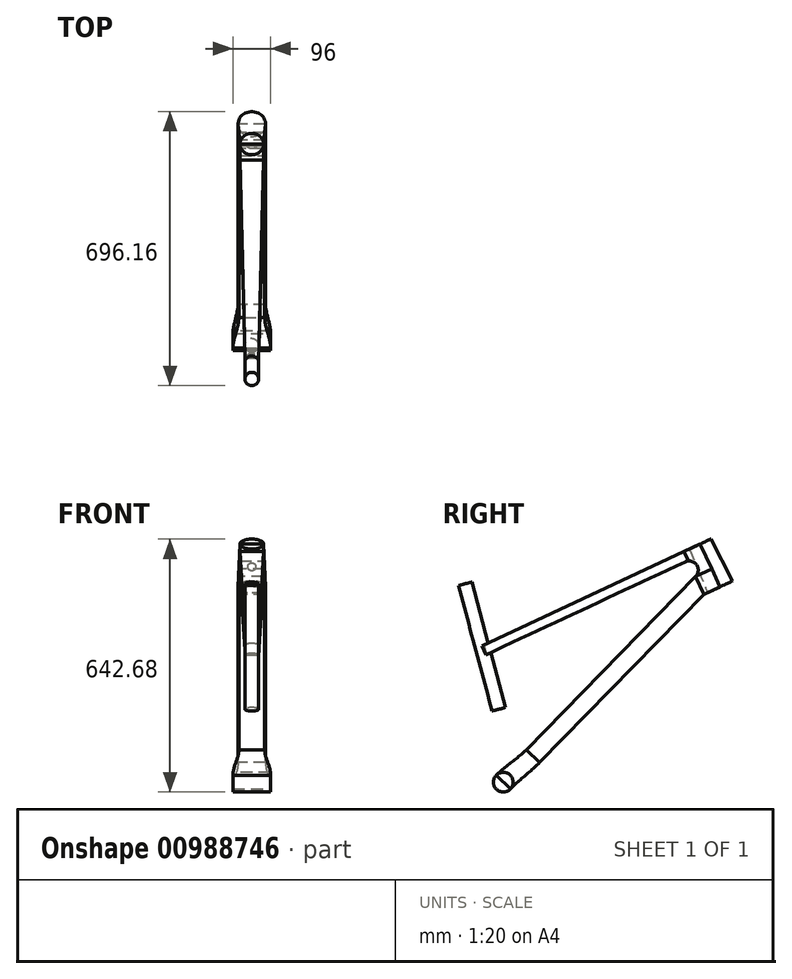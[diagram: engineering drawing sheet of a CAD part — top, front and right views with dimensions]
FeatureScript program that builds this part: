
annotation { "Feature Type Name" : "Feature", "Feature Type Description" : "" }
export const myFeature = defineFeature(function(context is Context, id is Id, definition is map)
    precondition{}
    {
        {
            var Q0;
            Q0=qCreatedBy(makeId("Right.planeOp"),FACE);
            var sketch = newSketch(context, id + "F0", { "sketchPlane" : qUnion([Q0])});
            skLineSegment(sketch, "E0", {"start": v(30, 30.68) * mm, "end": v(-96.82, 503.98) * mm});
            skCircle(sketch, "E1", {"center": v(0, 0) * mm, "radius": 25 * mm});
            skLineSegment(sketch, "E2", {"start": v(0, 0) * mm, "end": v(0, 605) * mm});
            skLineSegment(sketch, "E3", {"start": v(0, 605) * mm, "end": v(500, 605) * mm});
            skLineSegment(sketch, "E4", {"start": v(500, 605) * mm, "end": v(550.71, 496.24) * mm});
            skLineSegment(sketch, "E5", {"start": v(-123.89, 605) * mm, "end": v(500, 605) * mm});
            skLineSegment(sketch, "E6", {"start": v(0, 0) * mm, "end": v(991.3, 0) * mm});
            skLineSegment(sketch, "E7", {"start": v(-96.82, 503.98) * mm, "end": v(-123.89, 605) * mm});
            skLineSegment(sketch, "E8", {"start": v(550.71, 496.24) * mm, "end": v(590.6, 514.84) * mm});
            skLineSegment(sketch, "E9", {"start": v(590.6, 514.84) * mm, "end": v(825.14, 11.84) * mm});
            skLineSegment(sketch, "E10", {"start": v(0, 11.84) * mm, "end": v(-430, 11.84) * mm});
            skCircle(sketch, "E11", {"center": v(-430, 11.84) * mm, "radius": 300 * mm});
            skCircle(sketch, "E12", {"center": v(825.14, 11.84) * mm, "radius": 342 * mm});
            skLineSegment(sketch, "E13", {"start": v(500, 605) * mm, "end": v(-76.95, 429.84) * mm});
            skLineSegment(sketch, "E14", {"start": v(-537.8, -330.16) * mm, "end": v(1117.44, -330.16) * mm});
            skLineSegment(sketch, "E15", {"start": v(500, 605) * mm, "end": v(-54.6, 346.39) * mm});
            skCircle(sketch, "E16", {"center": v(-430, 11.84) * mm, "radius": 362.5 * mm});
            skLineSegment(sketch, "E17", {"start": v(-96.82, 503.98) * mm, "end": v(0, 11.84) * mm, "construction": true});
            skLineSegment(sketch, "E18", {"start": v(0, 0) * mm, "end": v(529.58, 541.56) * mm});
            skCircle(sketch, "E19", {"center": v(0, 0) * mm, "radius": 70 * mm, "construction": true});
            skSolve(sketch);
        }
        {
            var Q0;
            Q0=qCreatedBy(makeId("Right.planeOp"),FACE);
            var sketch = newSketch(context, id + "F1", { "sketchPlane" : qUnion([Q0])});
            skLineSegment(sketch, "E20", {"start": v(500, 605) * mm, "end": v(527.19, 617.68) * mm});
            skLineSegment(sketch, "E21", {"start": v(550.71, 496.24) * mm, "end": v(582.43, 511.03) * mm});
            skLineSegment(sketch, "E22", {"start": v(500, 605) * mm, "end": v(550.71, 496.24) * mm});
            skLineSegment(sketch, "E23", {"start": v(527.19, 617.68) * mm, "end": v(582.43, 511.03) * mm});
            skSolve(sketch);
        }
        {
            var Q0;
            Q0=sQuery(id+"F0.wireOp",EDGE,"E15");
            var Q1;
            Q1=sQuery(id+"F0.wireOp",VERTEX,"E3.end");
            cPlane(context, id + "F2", {"entities" : qUnion([Q0, Q1]), "cplaneType" : CPlaneType.LINE_POINT, "offset" : 25 * mm, "width" : 150 * mm, "height" : 150 * mm});
        }
        {
            var Q0;
            Q0=sQuery(id+"F0.wireOp",EDGE,"E18");
            var Q1;
            Q1=sQuery(id+"F0.wireOp",VERTEX,"E2.start");
            cPlane(context, id + "F3", {"entities" : qUnion([Q0, Q1]), "cplaneType" : CPlaneType.LINE_POINT, "offset" : 25 * mm, "width" : 150 * mm, "height" : 150 * mm});
        }
        {
            var Q0;
            Q0=qCreatedBy(id+"F3.planeOp",FACE);
            var sketch = newSketch(context, id + "F4", { "sketchPlane" : qUnion([Q0])});
            skLineSegment(sketch, "E24.bottom", {"start": v(-48, 25) * mm, "end": v(48, 25) * mm});
            skLineSegment(sketch, "E24.top", {"start": v(-48, -25) * mm, "end": v(48, -25) * mm});
            skLineSegment(sketch, "E24.left", {"start": v(-48, 25) * mm, "end": v(-48, -25) * mm});
            skLineSegment(sketch, "E24.right", {"start": v(48, 25) * mm, "end": v(48, -25) * mm});
            skPoint(sketch, "E24.middle", {"position": v(0, 0) * mm});
            skSolve(sketch);
        }
        {
            var Q0;
            Q0=sQuery(id+"F0.wireOp",VERTEX,"E0.end");
            var Q1;
            Q1=sQuery(id+"F0.wireOp",EDGE,"E0");
            cPlane(context, id + "F5", {"entities" : qUnion([Q0, Q1]), "cplaneType" : CPlaneType.LINE_POINT, "offset" : 25 * mm, "width" : 150 * mm, "height" : 150 * mm});
        }
        {
            var Q0;
            Q0=qCreatedBy(id+"F5.planeOp",FACE);
            var sketch = newSketch(context, id + "F6", { "sketchPlane" : qUnion([Q0])});
            skCircle(sketch, "E25", {"center": v(0, 36.92) * mm, "radius": 17.5 * mm});
            skSolve(sketch);
        }
        {
            var Q0;
            Q0 = qSketchRegion(id + "F1", true);
            var Q1;
            Q1=sQuery(id+"F1.wireOp",EDGE,"E23");
            var Q2;
            Q2=sQuery(id+"F0.wireOp",EDGE,"E4");
            revolve(context, id + "F7", {"surfaceOperationType" : NewSurfaceOperationType.NEW, "entities" : qUnion([Q0]), "surfaceEntities" : qUnion([Q1]), "axis" : qUnion([Q2]), "revolveType" : RevolveType.FULL});
        }
        {
            var Q0;
            {var subQ0=sQuery(id+"F0.wireOp",EDGE,"E2");var subQ1=sQuery(id+"F0.wireOp",EDGE,"E1");var subQ2=makeQuery(id+"F0.imprint","INTERSECT",VERTEX,{"derivedFrom":[subQ1,subQ0]});Q0=makeQuery(id+"F0.imprint","IMPRINT",FACE,{"disambiguationData":[TD([[makeQuery(id+"F0.imprint","IMPRINT",EDGE,{"disambiguationData":[TD([[subQ2,-1.0]])],"derivedFrom":subQ1}),1.0]])]});}
            var Q1;
            {var subQ0=sQuery(id+"F0.wireOp",EDGE,"E2");var subQ1=sQuery(id+"F0.wireOp",EDGE,"E1");var subQ2=makeQuery(id+"F0.imprint","INTERSECT",VERTEX,{"derivedFrom":[subQ1,subQ0]});Q1=makeQuery(id+"F0.imprint","IMPRINT",FACE,{"disambiguationData":[TD([[makeQuery(id+"F0.imprint","IMPRINT",EDGE,{"disambiguationData":[TD([[subQ2,1.0]])],"derivedFrom":subQ1}),1.0]])]});}
            var Q2;
            {var subQ0=sQuery(id+"F0.wireOp",EDGE,"E18");var subQ1=sQuery(id+"F0.wireOp",EDGE,"E1");var subQ2=makeQuery(id+"F0.imprint","INTERSECT",VERTEX,{"derivedFrom":[subQ1,subQ0]});Q2=makeQuery(id+"F0.imprint","IMPRINT",FACE,{"disambiguationData":[TD([[makeQuery(id+"F0.imprint","IMPRINT",EDGE,{"disambiguationData":[TD([[subQ2,1.0]])],"derivedFrom":subQ1}),1.0]])]});}
            var Q3;
            {var subQ0=sQuery(id+"F0.wireOp",EDGE,"E10");var subQ1=sQuery(id+"F0.wireOp",EDGE,"E1");var subQ2=makeQuery(id+"F0.imprint","INTERSECT",VERTEX,{"derivedFrom":[subQ1,subQ0]});Q3=makeQuery(id+"F0.imprint","IMPRINT",FACE,{"disambiguationData":[TD([[makeQuery(id+"F0.imprint","IMPRINT",EDGE,{"disambiguationData":[TD([[subQ2,-1.0]])],"derivedFrom":subQ1}),1.0]])]});}
            var Q4;
            Q4=sQuery(id+"F0.wireOp",EDGE,"E1");
            extrude(context, id + "F8", {"entities" : qUnion([Q0, Q1, Q2, Q3]), "surfaceEntities" : qUnion([Q4]), "endBound" : BoundingType.SYMMETRIC, "depth" : 96 * mm, "offsetDistance" : 25 * mm});
        }
        {
            var Q0;
            Q0=qCreatedBy(id+"F2.planeOp",FACE);
            var sketch = newSketch(context, id + "F9", { "sketchPlane" : qUnion([Q0])});
            skLineSegment(sketch, "E26", {"start": v(35, 217) * mm, "end": v(-35, 217) * mm});
            skLineSegment(sketch, "E27", {"start": v(-35, 217) * mm, "end": v(-32.92, 267) * mm});
            skLineSegment(sketch, "E28", {"start": v(-32.92, 267) * mm, "end": v(32.92, 267) * mm});
            skLineSegment(sketch, "E29", {"start": v(32.92, 267) * mm, "end": v(35, 217) * mm});
            skLineSegment(sketch, "E30", {"start": v(32.92, 267) * mm, "end": v(30, 337) * mm, "construction": true});
            skLineSegment(sketch, "E31", {"start": v(-32.92, 267) * mm, "end": v(-30, 337) * mm, "construction": true});
            skSolve(sketch);
        }
        {
            var Q0;
            Q0 = qSketchRegion(id + "F9", true);
            var Q1;
            Q1 = qConstructionFilter(qBodyType(qCreatedBy(id + "F9" ,EDGE), BodyType.WIRE), ConstructionObject.NO);
            extrude(context, id + "F10", {"entities" : qUnion([Q0]), "surfaceEntities" : qUnion([Q1]), "depth" : 45 * mm, "offsetDistance" : 25 * mm});
        }
        {
            var Q0;
            Q0=makeQuery(id+"F10.opExtrude","CAP_VERTEX",VERTEX,{"disambiguationData":[OSD([sQuery(id+"F9.wireOp",EDGE,"E27"),sQuery(id+"F9.wireOp",EDGE,"E28")])],"isStart":false});
            var Q1;
            Q1=makeQuery(id+"F10.opExtrude","CAP_VERTEX",VERTEX,{"disambiguationData":[OSD([sQuery(id+"F9.wireOp",EDGE,"E26"),sQuery(id+"F9.wireOp",EDGE,"E27")])],"isStart":false});
            var Q2;
            Q2=makeQuery(id+"F10.opExtrude","CAP_VERTEX",VERTEX,{"disambiguationData":[OSD([sQuery(id+"F9.wireOp",EDGE,"E28"),sQuery(id+"F9.wireOp",EDGE,"E29")])],"isStart":false});
            cPlane(context, id + "F11", {"entities" : qUnion([Q0, Q1, Q2]), "cplaneType" : CPlaneType.THREE_POINT, "offset" : 25 * mm, "width" : 150 * mm, "height" : 150 * mm});
        }
        {
            var Q0;
            Q0=qCreatedBy(id+"F11.planeOp",FACE);
            var sketch = newSketch(context, id + "F12", { "sketchPlane" : qUnion([Q0])});
            skLineSegment(sketch, "E32.0", {"start": v(32.92, 267) * mm, "end": v(-32.92, 267) * mm});
            skLineSegment(sketch, "E33.0", {"start": v(35, 217) * mm, "end": v(32.92, 267) * mm});
            skLineSegment(sketch, "E34.0", {"start": v(-35, 217) * mm, "end": v(35, 217) * mm});
            skLineSegment(sketch, "E35.0", {"start": v(-32.92, 267) * mm, "end": v(-35, 217) * mm});
            skSolve(sketch);
        }
        {
            var Q0;
            Q0=qCreatedBy(id+"F3.planeOp",FACE);
            cPlane(context, id + "F13", {"entities" : qUnion([Q0]), "cplaneType" : CPlaneType.OFFSET, "offset" : 100 * mm, "width" : 150 * mm, "height" : 150 * mm});
        }
        {
            var Q0;
            Q0=qCreatedBy(id+"F13.planeOp",FACE);
            var sketch = newSketch(context, id + "F14", { "sketchPlane" : qUnion([Q0])});
            skLineSegment(sketch, "E36.0", {"start": v(-32.92, -15.86) * mm, "end": v(32.92, -15.86) * mm});
            skLineSegment(sketch, "E37.0", {"start": v(-35, 30.93) * mm, "end": v(-32.92, -15.86) * mm});
            skLineSegment(sketch, "E38.0", {"start": v(35, 30.93) * mm, "end": v(-35, 30.93) * mm});
            skLineSegment(sketch, "E39.0", {"start": v(32.92, -15.86) * mm, "end": v(35, 30.93) * mm});
            skSolve(sketch);
        }
        {
            var Q0;
            Q0 = qSketchRegion(id + "F14", true);
            var Q1;
            Q1 = qSketchRegion(id + "F4", true);
            var Q2;
            Q2 = qConstructionFilter(qBodyType(qCreatedBy(id + "F14" ,EDGE), BodyType.WIRE), ConstructionObject.NO);
            var Q3;
            Q3 = qConstructionFilter(qBodyType(qCreatedBy(id + "F4" ,EDGE), BodyType.WIRE), ConstructionObject.NO);
            loft(context, id + "F15", {"startCondition" : LoftEndDerivativeType.NORMAL_TO_PROFILE, "startMagnitude" : 1, "endCondition" : LoftEndDerivativeType.NORMAL_TO_PROFILE, "endMagnitude" : 1, "sheetProfilesArray" : [{ "sheetProfileEntities" : qUnion([Q0]) }, { "sheetProfileEntities" : qUnion([Q1]) }], "wireProfilesArray" : [{ "wireProfileEntities" : qUnion([Q2]) }, { "wireProfileEntities" : qUnion([Q3]) }]});
        }
        {
            var Q0;
            Q0 = qSketchRegion(id + "F14", true);
            var Q1;
            Q1=makeQuery(id+"F12.imprint","IMPRINT",FACE,{"disambiguationData":[TD([[makeQuery(id+"F12.imprint","IMPRINT",EDGE,{"derivedFrom":sQuery(id+"F12.wireOp",EDGE,"E32.0")}),1.0]])]});
            var Q2;
            Q2 = qConstructionFilter(qBodyType(qCreatedBy(id + "F14" ,EDGE), BodyType.WIRE), ConstructionObject.NO);
            var Q3;
            Q3 = qConstructionFilter(qBodyType(qCreatedBy(id + "F12" ,EDGE), BodyType.WIRE), ConstructionObject.NO);
            loft(context, id + "F16", {"surfaceOperationType" : NewSurfaceOperationType.ADD, "sheetProfilesArray" : [{ "sheetProfileEntities" : qUnion([Q0]) }, { "sheetProfileEntities" : qUnion([Q1]) }], "wireProfilesArray" : [{ "wireProfileEntities" : qUnion([Q2]) }, { "wireProfileEntities" : qUnion([Q3]) }]});
        }
        {
            var Q0;
            Q0=makeQuery(id+"F6.imprint","IMPRINT",FACE,{"disambiguationData":[TD([[makeQuery(id+"F6.imprint","IMPRINT",EDGE,{"derivedFrom":sQuery(id+"F6.wireOp",EDGE,"E25")}),1.0]])]});
            var Q1;
            Q1=sQuery(id+"F6.wireOp",EDGE,"E25");
            extrude(context, id + "F17", {"entities" : qUnion([Q0]), "surfaceEntities" : qUnion([Q1]), "oppositeDirection" : true, "depth" : 330 * mm, "offsetDistance" : 25 * mm});
        }
        {
            var Q0;
            Q0=qCreatedBy(id+"F2.planeOp",FACE);
            var sketch = newSketch(context, id + "F18", { "sketchPlane" : qUnion([Q0])});
            skLineSegment(sketch, "E40", {"start": v(32.92, 267) * mm, "end": v(-32.92, 267) * mm});
            skLineSegment(sketch, "E41", {"start": v(-32.92, 267) * mm, "end": v(-30, 337) * mm});
            skLineSegment(sketch, "E42", {"start": v(-30, 337) * mm, "end": v(30, 337) * mm});
            skLineSegment(sketch, "E43", {"start": v(30, 337) * mm, "end": v(32.92, 267) * mm});
            skSolve(sketch);
        }
        {
            var Q0;
            Q0 = qSketchRegion(id + "F18", true);
            var Q1;
            Q1 = qConstructionFilter(qBodyType(qCreatedBy(id + "F18" ,EDGE), BodyType.WIRE), ConstructionObject.NO);
            extrude(context, id + "F19", {"entities" : qUnion([Q0]), "surfaceEntities" : qUnion([Q1]), "depth" : 45 * mm, "offsetDistance" : 25 * mm});
        }
        {
            var Q0;
            Q0=sQuery(id+"F0.wireOp",VERTEX,"E15.end");
            var Q1;
            Q1=sQuery(id+"F0.wireOp",EDGE,"E15");
            cPlane(context, id + "F20", {"entities" : qUnion([Q0, Q1]), "cplaneType" : CPlaneType.LINE_POINT, "offset" : 25 * mm, "width" : 150 * mm, "height" : 150 * mm});
        }
        {
            var Q0;
            Q0=qCreatedBy(id+"F20.planeOp",FACE);
            var sketch = newSketch(context, id + "F21", { "sketchPlane" : qUnion([Q0])});
            skLineSegment(sketch, "E44.bottom", {"start": v(-16.5, 337) * mm, "end": v(17.5, 337) * mm});
            skLineSegment(sketch, "E44.top", {"start": v(-16.5, 312) * mm, "end": v(17.5, 312) * mm});
            skLineSegment(sketch, "E44.left", {"start": v(-16.5, 337) * mm, "end": v(-16.5, 312) * mm});
            skLineSegment(sketch, "E44.right", {"start": v(17.5, 337) * mm, "end": v(17.5, 312) * mm});
            skSolve(sketch);
        }
        {
            var Q0;
            Q0=qCreatedBy(id+"F11.planeOp",FACE);
            var sketch = newSketch(context, id + "F22", { "sketchPlane" : qUnion([Q0])});
            skLineSegment(sketch, "E45.0", {"start": v(30, 337) * mm, "end": v(-30, 337) * mm});
            skLineSegment(sketch, "E46.0", {"start": v(32.92, 267) * mm, "end": v(30, 337) * mm});
            skLineSegment(sketch, "E47.0", {"start": v(-30, 337) * mm, "end": v(-32.92, 267) * mm});
            skLineSegment(sketch, "E48.0", {"start": v(32.92, 267) * mm, "end": v(-32.92, 267) * mm});
            skSolve(sketch);
        }
        {
            var Q0;
            Q0 = qSketchRegion(id + "F22", true);
            var Q1;
            Q1 = qSketchRegion(id + "F21", true);
            var Q2;
            Q2 = qConstructionFilter(qBodyType(qCreatedBy(id + "F22" ,EDGE), BodyType.WIRE), ConstructionObject.NO);
            var Q3;
            Q3 = qConstructionFilter(qBodyType(qCreatedBy(id + "F21" ,EDGE), BodyType.WIRE), ConstructionObject.NO);
            loft(context, id + "F23", {"sheetProfilesArray" : [{ "sheetProfileEntities" : qUnion([Q0]) }, { "sheetProfileEntities" : qUnion([Q1]) }], "wireProfilesArray" : [{ "wireProfileEntities" : qUnion([Q2]) }, { "wireProfileEntities" : qUnion([Q3]) }]});
        }
        {
            var Q0;
            Q0=makeQuery(id+"F23.opLoft","SWEPT_BODY",BODY,{"disambiguationData":[OSD([makeQuery(id+"F21.imprint","IMPRINT",FACE,{"disambiguationData":[TD([[makeQuery(id+"F21.imprint","IMPRINT",EDGE,{"derivedFrom":sQuery(id+"F21.wireOp",EDGE,"E44.bottom")}),-1.0]])]}),makeQuery(id+"F22.imprint","IMPRINT",FACE,{"disambiguationData":[TD([[makeQuery(id+"F22.imprint","IMPRINT",EDGE,{"derivedFrom":sQuery(id+"F22.wireOp",EDGE,"E45.0")}),1.0]])]})])]});
            var Q1;
            Q1=makeQuery(id+"F17.opExtrude","SWEPT_BODY",BODY,{"disambiguationData":[OSD([sQuery(id+"F6.wireOp",EDGE,"E25")])]});
            booleanBodies(context, id + "F24", {"operationType" : BooleanOperationType.UNION, "tools" : qUnion([Q0, Q1])});
        }
        {
            var Q0;
            Q0=qCreatedBy(makeId("Right.planeOp"),FACE);
            var sketch = newSketch(context, id + "F25", { "sketchPlane" : qUnion([Q0])});
            skLineSegment(sketch, "E49", {"start": v(-44.03, 323.73) * mm, "end": v(462.36, 559.86) * mm});
            skArc(sketch, "E50", {"start": v(488.8, 522.54) * mm, "mid": v(491.15, 552.23) * mm, "end": v(462.36, 559.86) * mm});
            skLineSegment(sketch, "E51", {"start": v(-44.03, 323.73) * mm, "end": v(488.8, 522.54) * mm});
            skSolve(sketch);
        }
        {
            var Q0;
            Q0 = qSketchRegion(id + "F25", true);
            extrude(context, id + "F26", {"entities" : qUnion([Q0]), "operationType" : NewBodyOperationType.REMOVE, "endBound" : BoundingType.SYMMETRIC, "oppositeDirection" : true, "depth" : 100 * mm, "offsetDistance" : 25 * mm});
        }
    });
